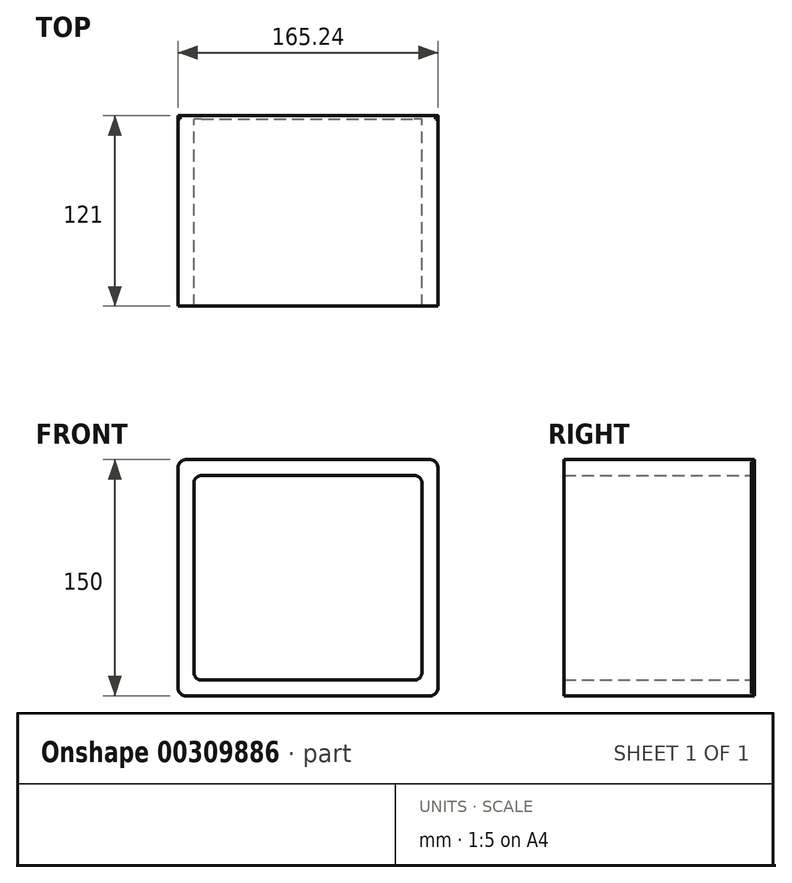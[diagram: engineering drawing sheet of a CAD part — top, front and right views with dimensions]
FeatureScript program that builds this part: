
annotation { "Feature Type Name" : "Feature", "Feature Type Description" : "" }
export const myFeature = defineFeature(function(context is Context, id is Id, definition is map)
    precondition{}
    {
        {
            var Q0;
            Q0=qCreatedBy(makeId("Front.planeOp"),FACE);
            var sketch = newSketch(context, id + "F0", { "sketchPlane" : qUnion([Q0])});
            skLineSegment(sketch, "E0.bottom", {"start": v(-77.5, 75) * mm, "end": v(77.5, 75) * mm});
            skLineSegment(sketch, "E0.top", {"start": v(-77.5, -75) * mm, "end": v(77.5, -75) * mm});
            skLineSegment(sketch, "E0.left", {"start": v(-82.5, 70) * mm, "end": v(-82.5, -70) * mm});
            skLineSegment(sketch, "E0.right", {"start": v(82.5, 70) * mm, "end": v(82.5, -70) * mm});
            skPoint(sketch, "E0.middle", {"position": v(0, 0) * mm});
            skLineSegment(sketch, "E1.bottom", {"start": v(-67.5, 65) * mm, "end": v(67.5, 65) * mm});
            skLineSegment(sketch, "E1.top", {"start": v(-67.5, -65) * mm, "end": v(67.5, -65) * mm});
            skLineSegment(sketch, "E1.left", {"start": v(-72.5, 60) * mm, "end": v(-72.5, -60) * mm});
            skLineSegment(sketch, "E1.right", {"start": v(72.5, 60) * mm, "end": v(72.5, -60) * mm});
            skPoint(sketch, "E2.visualSharp", {"position": v(-82.5, 75) * mm});
            skArc(sketch, "E2.filletArc", {"start": v(-77.5, 75) * mm, "mid": v(-81.04, 73.54) * mm, "end": v(-82.5, 70) * mm});
            skPoint(sketch, "E3.visualSharp", {"position": v(-72.5, 65) * mm});
            skArc(sketch, "E3.filletArc", {"start": v(-67.5, 65) * mm, "mid": v(-71.04, 63.54) * mm, "end": v(-72.5, 60) * mm});
            skPoint(sketch, "E4.visualSharp", {"position": v(-72.5, -65) * mm});
            skArc(sketch, "E4.filletArc", {"start": v(-72.5, -60) * mm, "mid": v(-71.04, -63.54) * mm, "end": v(-67.5, -65) * mm});
            skPoint(sketch, "E5.visualSharp", {"position": v(72.5, 65) * mm});
            skArc(sketch, "E5.filletArc", {"start": v(72.5, 60) * mm, "mid": v(71.04, 63.54) * mm, "end": v(67.5, 65) * mm});
            skPoint(sketch, "E6.visualSharp", {"position": v(82.5, 75) * mm});
            skArc(sketch, "E6.filletArc", {"start": v(82.5, 70) * mm, "mid": v(81.04, 73.54) * mm, "end": v(77.5, 75) * mm});
            skPoint(sketch, "E7.visualSharp", {"position": v(82.5, -75) * mm});
            skArc(sketch, "E7.filletArc", {"start": v(77.5, -75) * mm, "mid": v(81.04, -73.54) * mm, "end": v(82.5, -70) * mm});
            skPoint(sketch, "E8.visualSharp", {"position": v(72.5, -65) * mm});
            skArc(sketch, "E8.filletArc", {"start": v(67.5, -65) * mm, "mid": v(71.04, -63.54) * mm, "end": v(72.5, -60) * mm});
            skPoint(sketch, "E9.visualSharp", {"position": v(-82.5, -75) * mm});
            skArc(sketch, "E9.filletArc", {"start": v(-82.5, -70) * mm, "mid": v(-81.04, -73.54) * mm, "end": v(-77.5, -75) * mm});
            skSolve(sketch);
        }
        {
            var Q0;
            Q0 = qSketchRegion(id + "F0", true);
            extrude(context, id + "F1", {"entities" : qUnion([Q0]), "depth" : 121 * mm});
        }
        {
            var Q0;
            Q0=qCreatedBy(makeId("Front.planeOp"),FACE);
            var sketch = newSketch(context, id + "F2", { "sketchPlane" : qUnion([Q0])});
            skLineSegment(sketch, "E10.bottom", {"start": v(-77.62, 74.88) * mm, "end": v(77.62, 74.88) * mm});
            skLineSegment(sketch, "E10.top", {"start": v(-77.62, -74.88) * mm, "end": v(77.62, -74.88) * mm});
            skLineSegment(sketch, "E10.left", {"start": v(-82.62, 69.88) * mm, "end": v(-82.62, -69.88) * mm});
            skLineSegment(sketch, "E10.right", {"start": v(82.62, 69.88) * mm, "end": v(82.62, -69.88) * mm});
            skPoint(sketch, "E10.middle", {"position": v(0, 0) * mm});
            skPoint(sketch, "E11.visualSharp", {"position": v(-82.62, 74.88) * mm});
            skArc(sketch, "E11.filletArc", {"start": v(-77.62, 74.88) * mm, "mid": v(-81.16, 73.41) * mm, "end": v(-82.62, 69.88) * mm});
            skPoint(sketch, "E12.visualSharp", {"position": v(-82.62, -74.88) * mm});
            skArc(sketch, "E12.filletArc", {"start": v(-82.62, -69.88) * mm, "mid": v(-81.16, -73.41) * mm, "end": v(-77.62, -74.88) * mm});
            skPoint(sketch, "E13.visualSharp", {"position": v(82.62, 74.88) * mm});
            skArc(sketch, "E13.filletArc", {"start": v(82.62, 69.88) * mm, "mid": v(81.16, 73.41) * mm, "end": v(77.62, 74.88) * mm});
            skPoint(sketch, "E14.visualSharp", {"position": v(82.62, -74.88) * mm});
            skArc(sketch, "E14.filletArc", {"start": v(77.62, -74.88) * mm, "mid": v(81.16, -73.41) * mm, "end": v(82.62, -69.88) * mm});
            skSolve(sketch);
        }
        {
            var Q0;
            Q0 = qSketchRegion(id + "F2", true);
            extrude(context, id + "F3", {"entities" : qUnion([Q0]), "operationType" : NewBodyOperationType.ADD, "depth" : 2 * mm});
        }
    });
